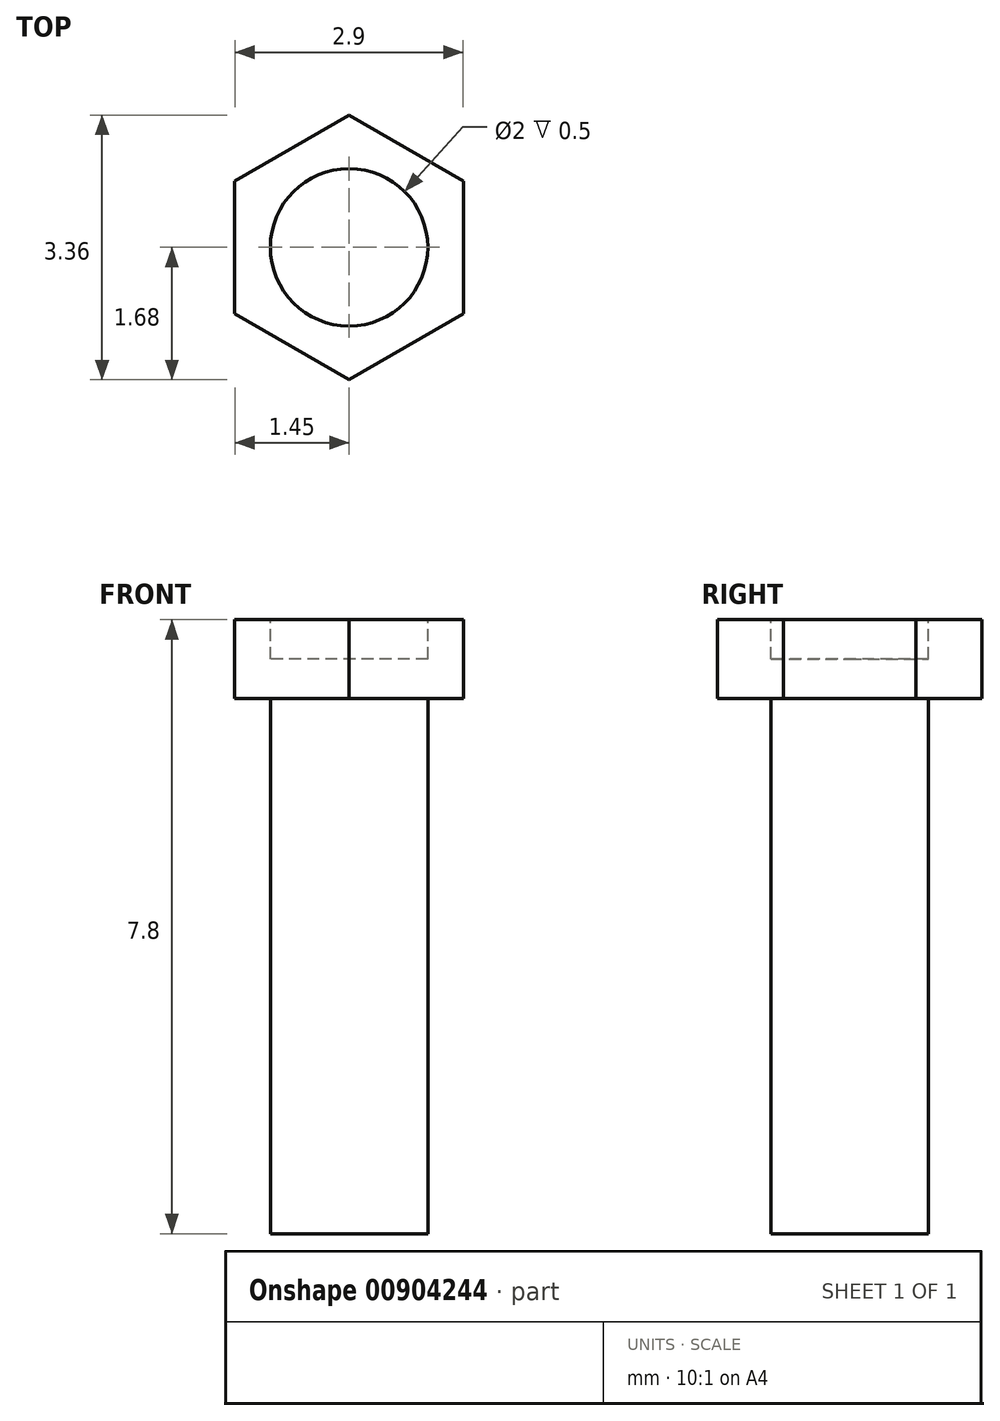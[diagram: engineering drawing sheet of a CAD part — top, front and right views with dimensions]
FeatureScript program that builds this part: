
annotation { "Feature Type Name" : "Feature", "Feature Type Description" : "" }
export const myFeature = defineFeature(function(context is Context, id is Id, definition is map)
    precondition{}
    {
        {
            var Q0;
            Q0=qCreatedBy(makeId("Front.planeOp"),FACE);
            var sketch = newSketch(context, id + "F0", { "sketchPlane" : qUnion([Q0])});
            skLineSegment(sketch, "E0.bottom", {"start": v(0, 0) * mm, "end": v(-1, 0) * mm});
            skLineSegment(sketch, "E0.top", {"start": v(0, 6.8) * mm, "end": v(-1, 6.8) * mm});
            skLineSegment(sketch, "E0.left", {"start": v(0, 0) * mm, "end": v(0, 6.8) * mm});
            skLineSegment(sketch, "E0.right", {"start": v(-1, 0) * mm, "end": v(-1, 6.8) * mm});
            skSolve(sketch);
        }
        {
            var Q0;
            Q0=makeQuery(id+"F0.imprint","IMPRINT",FACE,{"disambiguationData":[TD([[makeQuery(id+"F0.imprint","IMPRINT",EDGE,{"derivedFrom":sQuery(id+"F0.wireOp",EDGE,"E0.bottom")}),-1.0]])]});
            var Q1;
            Q1=sQuery(id+"F0.wireOp",EDGE,"E0.left");
            revolve(context, id + "F1", {"surfaceOperationType" : NewSurfaceOperationType.NEW, "entities" : qUnion([Q0]), "axis" : qUnion([Q1]), "revolveType" : RevolveType.FULL});
        }
        {
            var Q0;
            Q0=makeQuery(id+"F1.opRevolve","SWEPT_FACE",FACE,{"disambiguationData":[OSD([sQuery(id+"F0.wireOp",EDGE,"E0.top")])]});
            var sketch = newSketch(context, id + "F2", { "sketchPlane" : qUnion([Q0])});
            skLineSegment(sketch, "E1", {"start": v(0, 0) * mm, "end": v(0, 1.68) * mm});
            skCircle(sketch, "E2.cCircle", {"center": v(0, 0) * mm, "radius": 1.68 * mm, "construction": true});
            skLineSegment(sketch, "E2.0", {"start": v(0, 1.68) * mm, "end": v(1.45, 0.84) * mm});
            skLineSegment(sketch, "E2.1", {"start": v(1.45, 0.84) * mm, "end": v(1.45, -0.84) * mm});
            skLineSegment(sketch, "E2.2", {"start": v(1.45, -0.84) * mm, "end": v(0, -1.68) * mm});
            skLineSegment(sketch, "E2.3", {"start": v(0, -1.68) * mm, "end": v(-1.45, -0.84) * mm});
            skLineSegment(sketch, "E2.4", {"start": v(-1.45, -0.84) * mm, "end": v(-1.45, 0.84) * mm});
            skLineSegment(sketch, "E2.5", {"start": v(-1.45, 0.84) * mm, "end": v(0, 1.68) * mm});
            skSolve(sketch);
        }
        {
            var Q0;
            Q0=makeQuery(id+"F2.imprint","IMPRINT",FACE,{"disambiguationData":[TD([[makeQuery(id+"F2.imprint","IMPRINT",EDGE,{"derivedFrom":sQuery(id+"F2.wireOp",EDGE,"E2.0")}),-1.0]])]});
            var Q1;
            Q1=makeQuery(id+"F2.imprint","IMPRINT",FACE,{"disambiguationData":[TD([[makeQuery(id+"F2.imprint","IMPRINT",EDGE,{"derivedFrom":makeQuery(id+"F1.opRevolve","SWEPT_EDGE",EDGE,{"disambiguationData":[OSD([sQuery(id+"F0.wireOp",EDGE,"E0.top"),sQuery(id+"F0.wireOp",EDGE,"E0.right")])]})}),-1.0]])]});
            extrude(context, id + "F3", {"entities" : qUnion([Q0, Q1]), "operationType" : NewBodyOperationType.ADD, "depth" : 1 * mm, "offsetDistance" : 25 * mm});
        }
        {
            var Q0;
            Q0=makeQuery(id+"F3.opExtrude","CAP_FACE",FACE,{"disambiguationData":[OSD([sQuery(id+"F2.wireOp",EDGE,"E2.0"),sQuery(id+"F2.wireOp",EDGE,"E2.1"),sQuery(id+"F2.wireOp",EDGE,"E2.2"),sQuery(id+"F2.wireOp",EDGE,"E2.3"),sQuery(id+"F2.wireOp",EDGE,"E2.4"),sQuery(id+"F2.wireOp",EDGE,"E2.5")])],"isStart":false});
            var sketch = newSketch(context, id + "F4", { "sketchPlane" : qUnion([Q0])});
            skPoint(sketch, "E3.0", {"position": v(0, 0) * mm});
            skCircle(sketch, "E4", {"center": v(0, 0) * mm, "radius": 1 * mm});
            skSolve(sketch);
        }
        {
            var Q0;
            Q0=makeQuery(id+"F4.imprint","IMPRINT",FACE,{"disambiguationData":[TD([[makeQuery(id+"F4.imprint","IMPRINT",EDGE,{"derivedFrom":sQuery(id+"F4.wireOp",EDGE,"E4")}),1.0]])]});
            extrude(context, id + "F5", {"entities" : qUnion([Q0]), "operationType" : NewBodyOperationType.REMOVE, "oppositeDirection" : true, "depth" : 0.5 * mm, "offsetDistance" : 25 * mm});
        }
    });
